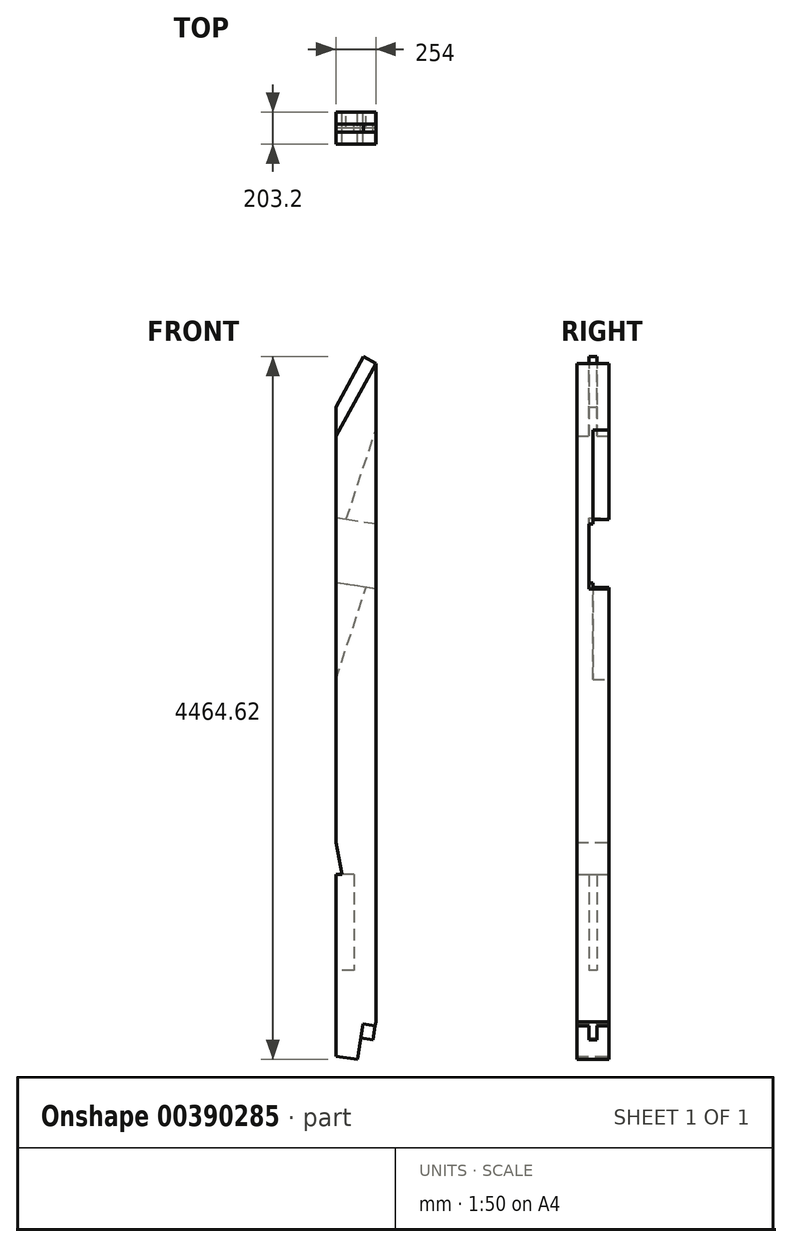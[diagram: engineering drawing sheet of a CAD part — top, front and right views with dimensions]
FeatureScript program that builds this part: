
annotation { "Feature Type Name" : "Feature", "Feature Type Description" : "" }
export const myFeature = defineFeature(function(context is Context, id is Id, definition is map)
    precondition{}
    {
        {
            var Q0;
            Q0=qCreatedBy(makeId("Front.planeOp"),FACE);
            var sketch = newSketch(context, id + "F0", { "sketchPlane" : qUnion([Q0])});
            skLineSegment(sketch, "E0.bottom", {"start": v(-127, 2356.61) * mm, "end": v(127, 2356.61) * mm});
            skLineSegment(sketch, "E0.top", {"start": v(-127, -2356.61) * mm, "end": v(127, -2356.61) * mm});
            skLineSegment(sketch, "E0.left", {"start": v(-127, 2356.61) * mm, "end": v(-127, -2356.61) * mm});
            skLineSegment(sketch, "E0.right", {"start": v(127, 2356.61) * mm, "end": v(127, -2356.61) * mm});
            skPoint(sketch, "E0.middle", {"position": v(0, 0) * mm});
            skLineSegment(sketch, "E1", {"start": v(127, 2276.75) * mm, "end": v(127, 1383.6) * mm});
            skLineSegment(sketch, "E2", {"start": v(127, -2356.61) * mm, "end": v(-127, -2316.99) * mm});
            skLineSegment(sketch, "E3", {"start": v(9.42, -2338.27) * mm, "end": v(127, -1584.57) * mm});
            skLineSegment(sketch, "E4", {"start": v(127, -2099.54) * mm, "end": v(-127, -2059.92) * mm});
            skLineSegment(sketch, "E5", {"start": v(127, -2099.54) * mm, "end": v(123.08, -2124.64) * mm});
            skLineSegment(sketch, "E6", {"start": v(123.08, -2124.64) * mm, "end": v(44.66, -2112.4) * mm});
            skLineSegment(sketch, "E7", {"start": v(123.08, -2124.64) * mm, "end": v(109.38, -2212.47) * mm});
            skLineSegment(sketch, "E8", {"start": v(109.38, -2212.47) * mm, "end": v(30.96, -2200.24) * mm});
            skLineSegment(sketch, "E9", {"start": v(-127, 1621.31) * mm, "end": v(127, 2083.53) * mm});
            skLineSegment(sketch, "E10", {"start": v(127, 2083.53) * mm, "end": v(49.09, 2126.35) * mm});
            skLineSegment(sketch, "E11", {"start": v(49.09, 2126.35) * mm, "end": v(-127, 1805.9) * mm});
            skLineSegment(sketch, "E12", {"start": v(-127, -1162.25) * mm, "end": v(-88.9, -1162.25) * mm});
            skLineSegment(sketch, "E13", {"start": v(-88.9, -1162.25) * mm, "end": v(-127, -959.05) * mm});
            skSolve(sketch);
        }
        {
            var Q0;
            {var subQ0=sQuery(id+"F0.wireOp",EDGE,"E1");var subQ1=sQuery(id+"F0.wireOp",EDGE,"sLSA05CJ-ji3h-L38E-weDl-Nbee3Jkvs57l");var subQ2=makeQuery(id+"F0.imprint","INTERSECT",VERTEX,{"derivedFrom":[subQ1,subQ0]});Q0=makeQuery(id+"F0.imprint","IMPRINT",FACE,{"disambiguationData":[TD([[makeQuery(id+"F0.imprint","IMPRINT",EDGE,{"disambiguationData":[TD([[subQ2,1.0]])],"derivedFrom":subQ1}),-1.0]])]});}
            var Q1;
            {var subQ3=sQuery(id+"F0.wireOp",EDGE,"E2");var subQ5=sQuery(id+"F0.wireOp",EDGE,"E0.left");var subQ6=makeQuery(id+"F0.imprint","INTERSECT",VERTEX,{"derivedFrom":[subQ5,subQ3]});Q1=makeQuery(id+"F0.imprint","IMPRINT",FACE,{"disambiguationData":[TD([[makeQuery(id+"F0.imprint","IMPRINT",EDGE,{"disambiguationData":[TD([[subQ6,1.0]])],"derivedFrom":subQ5}),1.0]])]});}
            var Q2;
            {var subQ4=sQuery(id+"F0.wireOp",EDGE,"E5");Q2=makeQuery(id+"F0.imprint","IMPRINT",FACE,{"disambiguationData":[TD([[makeQuery(id+"F0.imprint","IMPRINT",EDGE,{"derivedFrom":subQ4}),-1.0]])]});}
            var Q3;
            {var subQ0=sQuery(id+"F0.wireOp",EDGE,"E3");var subQ1=sQuery(id+"F0.wireOp",EDGE,"E0.right");var subQ2=makeQuery(id+"F0.imprint","INTERSECT",VERTEX,{"derivedFrom":[subQ1,subQ0]});Q3=makeQuery(id+"F0.imprint","IMPRINT",FACE,{"disambiguationData":[TD([[makeQuery(id+"F0.imprint","IMPRINT",EDGE,{"disambiguationData":[TD([[subQ2,1.0]])],"derivedFrom":subQ0}),-1.0]])]});}
            var Q4;
            {var subQ1=sQuery(id+"F0.wireOp",EDGE,"E0.right");var subQ8=sQuery(id+"F0.wireOp",EDGE,"E3");var subQ10=makeQuery(id+"F0.imprint","INTERSECT",VERTEX,{"derivedFrom":[subQ1,subQ8]});Q4=makeQuery(id+"F0.imprint","IMPRINT",FACE,{"disambiguationData":[TD([[makeQuery(id+"F0.imprint","IMPRINT",EDGE,{"disambiguationData":[TD([[subQ10,1.0]])],"derivedFrom":subQ8}),1.0]])]});}
            var Q5;
            {var subQ0=sQuery(id+"F0.wireOp",EDGE,"AvJj18g5-EUTS-k4jc-6ocs-XMw9zm4LYAZX");var subQ3=sQuery(id+"F0.wireOp",EDGE,"mu8KSUqH-O1Wu-QaL4-81EO-u4Yjg0J5JKGk");var subQ5=makeQuery(id+"F0.imprint","INTERSECT",VERTEX,{"derivedFrom":[subQ0,subQ3]});Q5=makeQuery(id+"F0.imprint","IMPRINT",FACE,{"disambiguationData":[TD([[makeQuery(id+"F0.imprint","IMPRINT",EDGE,{"disambiguationData":[TD([[subQ5,-1.0]])],"derivedFrom":subQ3}),1.0]])]});}
            extrude(context, id + "F1", {"entities" : qUnion([Q0, Q1, Q2, Q3, Q4, Q5]), "endBound" : BoundingType.SYMMETRIC, "depth" : 203.2 * mm});
        }
        {
            var Q0;
            {var subQ5=sQuery(id+"F0.wireOp",EDGE,"PrpMXbKC-m7py-lFAp-eg77-8aCVWW5FYuo4");Q0=makeQuery(id+"F0.imprint","IMPRINT",FACE,{"disambiguationData":[TD([[makeQuery(id+"F0.imprint","IMPRINT",EDGE,{"derivedFrom":subQ5}),-1.0]])]});}
            var Q1;
            {var subQ0=sQuery(id+"F0.wireOp",EDGE,"E6");Q1=makeQuery(id+"F0.imprint","IMPRINT",FACE,{"disambiguationData":[TD([[makeQuery(id+"F0.imprint","IMPRINT",EDGE,{"derivedFrom":subQ0}),1.0]])]});}
            var Q2;
            {var subQ0=sQuery(id+"F0.wireOp",EDGE,"0DDyUR7v-NsTs-4WLy-QZPT-bglCjnublC9u");Q2=makeQuery(id+"F0.imprint","IMPRINT",FACE,{"disambiguationData":[TD([[makeQuery(id+"F0.imprint","IMPRINT",EDGE,{"derivedFrom":subQ0}),-1.0]])]});}
            var Q3;
            Q3=makeQuery(id+"F0.imprint","IMPRINT",FACE,{"disambiguationData":[TD([[makeQuery(id+"F0.imprint","IMPRINT",EDGE,{"derivedFrom":sQuery(id+"F0.wireOp",EDGE,"0DDyUR7v-NsTs-4WLy-QZPT-bglCjnublC9u")}),1.0]])]});
            var Q4;
            {var subQ0=sQuery(id+"F0.wireOp",EDGE,"E1");var subQ5=sQuery(id+"F0.wireOp",EDGE,"sLSA05CJ-ji3h-L38E-weDl-Nbee3Jkvs57l");var subQ6=makeQuery(id+"F0.imprint","INTERSECT",VERTEX,{"derivedFrom":[subQ5,subQ0]});Q4=makeQuery(id+"F0.imprint","IMPRINT",FACE,{"disambiguationData":[TD([[makeQuery(id+"F0.imprint","IMPRINT",EDGE,{"disambiguationData":[TD([[subQ6,1.0]])],"derivedFrom":subQ5}),1.0]])]});}
            var Q5;
            {var subQ0=sQuery(id+"F0.wireOp",EDGE,"E9");Q5=makeQuery(id+"F0.imprint","IMPRINT",FACE,{"disambiguationData":[TD([[makeQuery(id+"F0.imprint","IMPRINT",EDGE,{"derivedFrom":subQ0}),1.0]])]});}
            extrude(context, id + "F2", {"entities" : qUnion([Q0, Q1, Q2, Q3, Q4, Q5]), "operationType" : NewBodyOperationType.ADD, "endBound" : BoundingType.SYMMETRIC, "depth" : 50.8 * mm});
        }
        {
            var Q0;
            Q0=makeQuery(id+"F1.opExtrude","CAP_FACE",FACE,{"disambiguationData":[OSD([sQuery(id+"F0.wireOp",EDGE,"E0.left"),sQuery(id+"F0.wireOp",EDGE,"E0.right"),sQuery(id+"F0.wireOp",EDGE,"sLSA05CJ-ji3h-L38E-weDl-Nbee3Jkvs57l"),sQuery(id+"F0.wireOp",EDGE,"AvJj18g5-EUTS-k4jc-6ocs-XMw9zm4LYAZX"),sQuery(id+"F0.wireOp",EDGE,"E1"),sQuery(id+"F0.wireOp",EDGE,"E2"),sQuery(id+"F0.wireOp",EDGE,"E3"),sQuery(id+"F0.wireOp",EDGE,"E5"),sQuery(id+"F0.wireOp",EDGE,"E6"),sQuery(id+"F0.wireOp",EDGE,"mu8KSUqH-O1Wu-QaL4-81EO-u4Yjg0J5JKGk")])],"isStart":true});
            var sketch = newSketch(context, id + "F3", { "sketchPlane" : qUnion([Q0])});
            skLineSegment(sketch, "E14", {"start": v(-127, 650.31) * mm, "end": v(127, 650.31) * mm});
            skLineSegment(sketch, "E15", {"start": v(-127, 650.31) * mm, "end": v(127, 689.96) * mm});
            skLineSegment(sketch, "E16", {"start": v(-127, 1061.64) * mm, "end": v(127, 1101.28) * mm});
            skLineSegment(sketch, "E17", {"start": v(-127, 855.97) * mm, "end": v(127, 895.62) * mm});
            skLineSegment(sketch, "E18", {"start": v(-127, 855.97) * mm, "end": v(127, -771.19) * mm});
            skLineSegment(sketch, "E19", {"start": v(150.66, 3.73) * mm, "end": v(-129.44, 855.6) * mm});
            skLineSegment(sketch, "E20", {"start": v(131.39, 877.03) * mm, "end": v(-127, 1661.14) * mm});
            skSolve(sketch);
        }
        {
            var Q0;
            {var subQ5=sQuery(id+"F3.wireOp",EDGE,"E17");Q0=makeQuery(id+"F3.imprint","IMPRINT",FACE,{"disambiguationData":[TD([[makeQuery(id+"F3.imprint","IMPRINT",EDGE,{"derivedFrom":subQ5}),-1.0]])]});}
            var Q1;
            {var subQ5=sQuery(id+"F3.wireOp",EDGE,"E17");Q1=makeQuery(id+"F3.imprint","IMPRINT",FACE,{"disambiguationData":[TD([[makeQuery(id+"F3.imprint","IMPRINT",EDGE,{"derivedFrom":subQ5}),1.0]])]});}
            var Q2;
            {var subQ0=sQuery(id+"F3.wireOp",EDGE,"E16");var subQ1=makeQuery(id+"F1.opExtrude","CAP_EDGE",EDGE,{"disambiguationData":[OSD([sQuery(id+"F0.wireOp",EDGE,"E0.left")])],"isStart":true});var subQ2=makeQuery(id+"F3.imprint","INTERSECT",VERTEX,{"derivedFrom":[subQ1,subQ0]});Q2=makeQuery(id+"F3.imprint","IMPRINT",FACE,{"disambiguationData":[TD([[makeQuery(id+"F3.imprint","IMPRINT",EDGE,{"disambiguationData":[TD([[subQ2,1.0]])],"derivedFrom":subQ0}),-1.0]])]});}
            var Q3;
            {var subQ6=sQuery(id+"F3.wireOp",EDGE,"3UwuMON8-zLGd-AdFu-rX66-01Td6ad8YWXp");var subQ8=sQuery(id+"F3.wireOp",EDGE,"E15");var subQ9=makeQuery(id+"F3.imprint","INTERSECT",VERTEX,{"derivedFrom":[subQ8,subQ6]});Q3=makeQuery(id+"F3.imprint","IMPRINT",FACE,{"disambiguationData":[TD([[makeQuery(id+"F3.imprint","IMPRINT",EDGE,{"disambiguationData":[TD([[subQ9,-1.0]])],"derivedFrom":subQ8}),1.0]])]});}
            var Q4;
            {var subQ0=sQuery(id+"F3.wireOp",EDGE,"E18");var subQ1=sQuery(id+"F3.wireOp",EDGE,"E15");var subQ2=makeQuery(id+"F3.imprint","INTERSECT",VERTEX,{"derivedFrom":[subQ1,subQ0]});Q4=makeQuery(id+"F3.imprint","IMPRINT",FACE,{"disambiguationData":[TD([[makeQuery(id+"F3.imprint","IMPRINT",EDGE,{"disambiguationData":[TD([[subQ2,-1.0]])],"derivedFrom":subQ1}),1.0]])]});}
            var Q5;
            {var subQ0=sQuery(id+"F3.wireOp",EDGE,"E15");var subQ3=sQuery(id+"F3.wireOp",EDGE,"E18");var subQ4=makeQuery(id+"F3.imprint","INTERSECT",VERTEX,{"derivedFrom":[subQ0,subQ3]});Q5=makeQuery(id+"F3.imprint","IMPRINT",FACE,{"disambiguationData":[TD([[makeQuery(id+"F3.imprint","IMPRINT",EDGE,{"disambiguationData":[TD([[subQ4,1.0]])],"derivedFrom":subQ3}),-1.0]])]});}
            var Q6;
            {var subQ0=sQuery(id+"F3.wireOp",EDGE,"E19");var subQ1=sQuery(id+"F3.wireOp",EDGE,"E15");var subQ2=makeQuery(id+"F3.imprint","INTERSECT",VERTEX,{"derivedFrom":[subQ1,subQ0]});Q6=makeQuery(id+"F3.imprint","IMPRINT",FACE,{"disambiguationData":[TD([[makeQuery(id+"F3.imprint","IMPRINT",EDGE,{"disambiguationData":[TD([[subQ2,-1.0]])],"derivedFrom":subQ1}),1.0]])]});}
            var Q7;
            {var subQ0=sQuery(id+"F3.wireOp",EDGE,"E18");var subQ3=sQuery(id+"F3.wireOp",EDGE,"E19");var subQ4=makeQuery(id+"F3.imprint","INTERSECT",VERTEX,{"derivedFrom":[subQ0,subQ3]});Q7=makeQuery(id+"F3.imprint","IMPRINT",FACE,{"disambiguationData":[TD([[makeQuery(id+"F3.imprint","IMPRINT",EDGE,{"disambiguationData":[TD([[subQ4,-1.0]])],"derivedFrom":subQ3}),-1.0]])]});}
            extrude(context, id + "F4", {"entities" : qUnion([Q0, Q1, Q2, Q3, Q4, Q5, Q6, Q7]), "operationType" : NewBodyOperationType.REMOVE, "oppositeDirection" : true, "depth" : 127 * mm});
        }
        {
            var Q0;
            {var subQ0=sQuery(id+"F3.wireOp",EDGE,"E14");var subQ1=makeQuery(id+"F1.opExtrude","CAP_EDGE",EDGE,{"disambiguationData":[OSD([sQuery(id+"F0.wireOp",EDGE,"E0.left")])],"isStart":true});var subQ2=makeQuery(id+"F3.imprint","INTERSECT",VERTEX,{"derivedFrom":[subQ1,subQ0]});Q0=makeQuery(id+"F3.imprint","IMPRINT",FACE,{"disambiguationData":[TD([[makeQuery(id+"F3.imprint","IMPRINT",EDGE,{"disambiguationData":[TD([[subQ2,1.0]])],"derivedFrom":subQ0}),-1.0]])]});}
            var Q1;
            {var subQ0=sQuery(id+"F3.wireOp",EDGE,"E14");var subQ1=makeQuery(id+"F1.opExtrude","CAP_EDGE",EDGE,{"disambiguationData":[OSD([sQuery(id+"F0.wireOp",EDGE,"E0.left")])],"isStart":true});var subQ2=makeQuery(id+"F3.imprint","INTERSECT",VERTEX,{"derivedFrom":[subQ1,subQ0]});Q1=makeQuery(id+"F3.imprint","IMPRINT",FACE,{"disambiguationData":[TD([[makeQuery(id+"F3.imprint","IMPRINT",EDGE,{"disambiguationData":[TD([[subQ2,1.0]])],"derivedFrom":subQ0}),1.0]])]});}
            var Q2;
            {var subQ0=sQuery(id+"F3.wireOp",EDGE,"E16");var subQ3=sQuery(id+"F3.wireOp",EDGE,"E20");var subQ4=makeQuery(id+"F3.imprint","INTERSECT",VERTEX,{"derivedFrom":[subQ0,subQ3]});Q2=makeQuery(id+"F3.imprint","IMPRINT",FACE,{"disambiguationData":[TD([[makeQuery(id+"F3.imprint","IMPRINT",EDGE,{"disambiguationData":[TD([[subQ4,1.0]])],"derivedFrom":subQ0}),1.0]])]});}
            var Q3;
            {var subQ0=sQuery(id+"F3.wireOp",EDGE,"E19");var subQ1=sQuery(id+"F3.wireOp",EDGE,"E14");var subQ2=makeQuery(id+"F3.imprint","INTERSECT",VERTEX,{"derivedFrom":[subQ1,subQ0]});Q3=makeQuery(id+"F3.imprint","IMPRINT",FACE,{"disambiguationData":[TD([[makeQuery(id+"F3.imprint","IMPRINT",EDGE,{"disambiguationData":[TD([[subQ2,-1.0]])],"derivedFrom":subQ1}),-1.0]])]});}
            var Q4;
            {var subQ0=sQuery(id+"F3.wireOp",EDGE,"E19");var subQ1=sQuery(id+"F3.wireOp",EDGE,"E14");var subQ2=makeQuery(id+"F3.imprint","INTERSECT",VERTEX,{"derivedFrom":[subQ1,subQ0]});Q4=makeQuery(id+"F3.imprint","IMPRINT",FACE,{"disambiguationData":[TD([[makeQuery(id+"F3.imprint","IMPRINT",EDGE,{"disambiguationData":[TD([[subQ2,-1.0]])],"derivedFrom":subQ1}),1.0]])]});}
            extrude(context, id + "F5", {"entities" : qUnion([Q0, Q1, Q2, Q3, Q4]), "operationType" : NewBodyOperationType.REMOVE, "oppositeDirection" : true, "depth" : 101.6 * mm});
        }
        {
            var Q0;
            {var subQ0=sQuery(id+"F0.wireOp",EDGE,"E0.left");var subQ1=makeQuery(id+"F0.imprint","INTERSECT",VERTEX,{"derivedFrom":[subQ0,sQuery(id+"F0.wireOp",EDGE,"E4")]});Q0=makeQuery(id+"F1.opExtrude","SWEPT_FACE",FACE,{"disambiguationData":[OSD([subQ0]),TDD([makeQuery(id+"F0.imprint","IMPRINT",EDGE,{"disambiguationData":[TD([[subQ1,1.0]])],"derivedFrom":subQ0}),makeQuery(id+"F0.imprint","IMPRINT",EDGE,{"disambiguationData":[TD([[makeQuery(id+"F0.imprint","INTERSECT",VERTEX,{"derivedFrom":[subQ0,sQuery(id+"F0.wireOp",EDGE,"E2")]}),1.0]])],"derivedFrom":subQ0})])]});}
            var sketch = newSketch(context, id + "F6", { "sketchPlane" : qUnion([Q0])});
            skLineSegment(sketch, "E21.bottom", {"start": v(-25.4, -1162.25) * mm, "end": v(25.4, -1162.25) * mm});
            skLineSegment(sketch, "E21.top", {"start": v(-25.4, -1771.85) * mm, "end": v(25.4, -1771.85) * mm});
            skLineSegment(sketch, "E21.left", {"start": v(-25.4, -1162.25) * mm, "end": v(-25.4, -1771.85) * mm});
            skLineSegment(sketch, "E21.right", {"start": v(25.4, -1162.25) * mm, "end": v(25.4, -1771.85) * mm});
            skPoint(sketch, "E21.middle", {"position": v(0, -1467.05) * mm});
            skSolve(sketch);
        }
        {
            var Q0;
            Q0=makeQuery(id+"F6.imprint","IMPRINT",FACE,{"disambiguationData":[TD([[makeQuery(id+"F6.imprint","IMPRINT",EDGE,{"derivedFrom":sQuery(id+"F6.wireOp",EDGE,"E21.bottom")}),1.0]])]});
            extrude(context, id + "F7", {"entities" : qUnion([Q0]), "operationType" : NewBodyOperationType.REMOVE, "oppositeDirection" : true, "depth" : 114.3 * mm, "offsetDistance" : 25.4 * mm});
        }
    });
